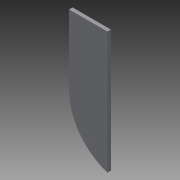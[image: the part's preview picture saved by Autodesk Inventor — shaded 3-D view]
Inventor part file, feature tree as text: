
AUTODESK INVENTOR PART (.ipt)
format: ipt  version: 2015 (Build 190159000, 159)  size: 82,944 bytes
history: native  units: mm
features: extrude x1, sketch x1
ambient origin geometry x8: Origin, YZ Plane, XZ Plane, XY Plane, X Axis, Y Axis, Z Axis, Center Point
bodies: Solid1 (feature_tree)
feature tree (2):
  extrude  "Extrusion1"  Depth=2.0mm
  sketch  "Sketch1"  dims[d0=22.0mm d1=30.0mm d2=25.0mm d3=15.0mm d4=0.2mm d5=8.0mm d8=0.2mm d10=0.2mm d11=2.0mm d12=0.0mm]
